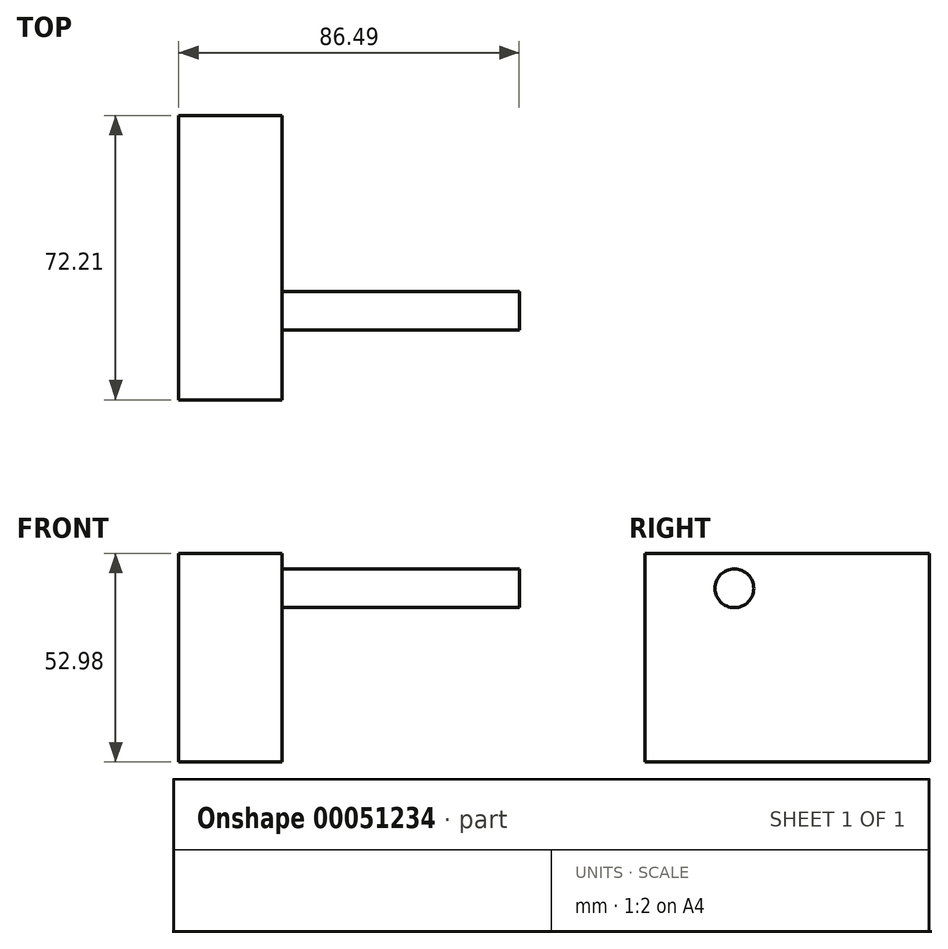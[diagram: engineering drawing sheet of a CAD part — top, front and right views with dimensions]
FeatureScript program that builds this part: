
annotation { "Feature Type Name" : "Feature", "Feature Type Description" : "" }
export const myFeature = defineFeature(function(context is Context, id is Id, definition is map)
    precondition{}
    {
        {
            var Q0;
            Q0=qCreatedBy(makeId("Top.planeOp"),FACE);
            var sketch = newSketch(context, id + "F0", { "sketchPlane" : qUnion([Q0])});
            skLineSegment(sketch, "E0.bottom", {"start": v(-41.74, 37.14) * mm, "end": v(44.75, 37.14) * mm});
            skLineSegment(sketch, "E0.top", {"start": v(-41.74, -35.07) * mm, "end": v(44.75, -35.07) * mm});
            skLineSegment(sketch, "E0.left", {"start": v(-41.74, 37.14) * mm, "end": v(-41.74, -35.07) * mm});
            skLineSegment(sketch, "E0.right", {"start": v(44.75, 37.14) * mm, "end": v(44.75, -35.07) * mm});
            skSolve(sketch);
        }
        {
            var Q0;
            Q0=makeQuery(id+"F0.imprint","IMPRINT",FACE,{"disambiguationData":[TD([[makeQuery(id+"F0.imprint","IMPRINT",EDGE,{"derivedFrom":sQuery(id+"F0.wireOp",EDGE,"E0.bottom")}),-1.0]])]});
            extrude(context, id + "F1", {"entities" : qUnion([Q0]), "depth" : 52.98 * mm});
        }
        {
            var Q0;
            Q0=makeQuery(id+"F1.opExtrude","SWEPT_FACE",FACE,{"disambiguationData":[OSD([sQuery(id+"F0.wireOp",EDGE,"E0.right")])]});
            var sketch = newSketch(context, id + "F2", { "sketchPlane" : qUnion([Q0])});
            skCircle(sketch, "E1", {"center": v(-12.41, 44.1) * mm, "radius": 4.92 * mm});
            skSolve(sketch);
        }
        {
            var Q0;
            Q0=makeQuery(id+"F2.imprint","IMPRINT",FACE,{"disambiguationData":[TD([[makeQuery(id+"F2.imprint","IMPRINT",EDGE,{"derivedFrom":sQuery(id+"F2.wireOp",EDGE,"E1")}),-1.0]])]});
            extrude(context, id + "F3", {"entities" : qUnion([Q0]), "operationType" : NewBodyOperationType.REMOVE, "oppositeDirection" : true, "depth" : 60.28 * mm});
        }
    });
